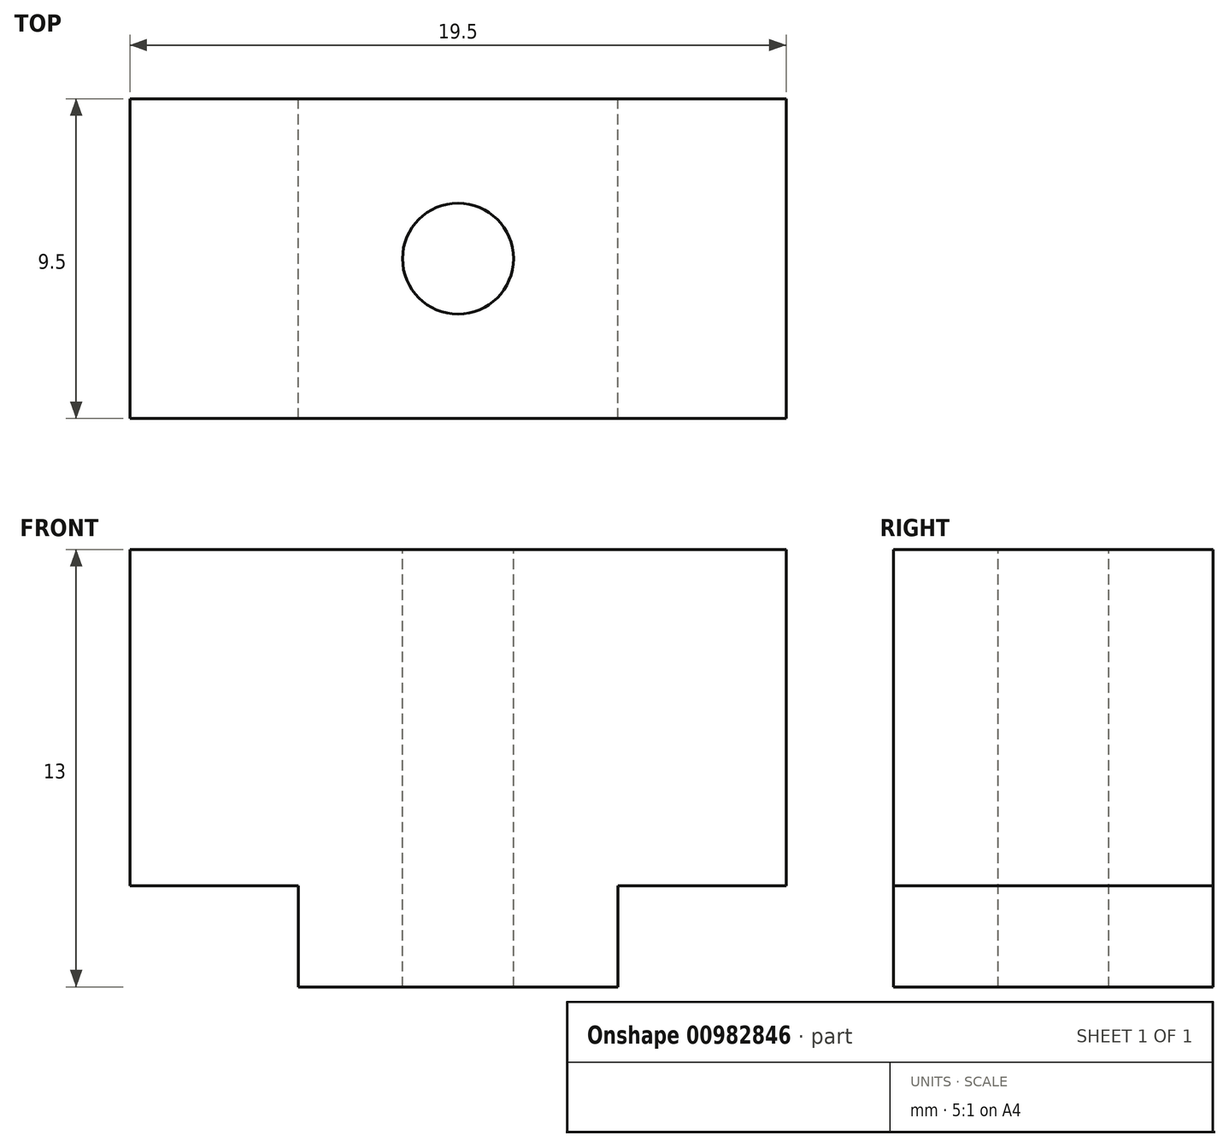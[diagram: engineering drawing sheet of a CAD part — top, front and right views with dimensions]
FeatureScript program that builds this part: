
annotation { "Feature Type Name" : "Feature", "Feature Type Description" : "" }
export const myFeature = defineFeature(function(context is Context, id is Id, definition is map)
    precondition{}
    {
        {
            var Q0;
            Q0=qCreatedBy(makeId("Front.planeOp"),FACE);
            var sketch = newSketch(context, id + "F0", { "sketchPlane" : qUnion([Q0])});
            skLineSegment(sketch, "E0", {"start": v(0, 10) * mm, "end": v(-9.75, 10) * mm});
            skLineSegment(sketch, "E1", {"start": v(-9.75, 10) * mm, "end": v(-9.75, 0) * mm});
            skLineSegment(sketch, "E2", {"start": v(-9.75, 0) * mm, "end": v(-4.75, 0) * mm});
            skLineSegment(sketch, "E3", {"start": v(-4.75, 0) * mm, "end": v(-4.75, -3) * mm});
            skLineSegment(sketch, "E4", {"start": v(-4.75, -3) * mm, "end": v(0, -3) * mm});
            skLineSegment(sketch, "E5.MirrorCS", {"start": v(0, 10) * mm, "end": v(9.75, 10) * mm});
            skLineSegment(sketch, "E6.MirrorCS", {"start": v(9.75, 10) * mm, "end": v(9.75, 0) * mm});
            skLineSegment(sketch, "E7.MirrorCS", {"start": v(9.75, 0) * mm, "end": v(4.75, 0) * mm});
            skLineSegment(sketch, "E8.MirrorCS", {"start": v(4.75, 0) * mm, "end": v(4.75, -3) * mm});
            skLineSegment(sketch, "E9.MirrorCS", {"start": v(4.75, -3) * mm, "end": v(0, -3) * mm});
            skSolve(sketch);
        }
        {
            var Q0;
            Q0 = qSketchRegion(id + "F0", true);
            extrude(context, id + "F1", {"entities" : qUnion([Q0]), "depth" : 9.5 * mm, "offsetDistance" : 25 * mm});
        }
        {
            var Q0;
            Q0=makeQuery(id+"F1.opExtrude","SWEPT_FACE",FACE,{"disambiguationData":[OSD([sQuery(id+"F0.wireOp",EDGE,"E0"),sQuery(id+"F0.wireOp",EDGE,"E5.MirrorCS")])]});
            var sketch = newSketch(context, id + "F2", { "sketchPlane" : qUnion([Q0])});
            skLineSegment(sketch, "E10", {"start": v(-9.75, 0) * mm, "end": v(9.75, -9.5) * mm, "construction": true});
            skLineSegment(sketch, "E11", {"start": v(9.75, 0) * mm, "end": v(-9.75, -9.5) * mm, "construction": true});
            skPoint(sketch, "E12", {"position": v(0, -4.75) * mm});
            skCircle(sketch, "E13", {"center": v(0, -4.75) * mm, "radius": 1.65 * mm});
            skSolve(sketch);
        }
        {
            var Q0;
            Q0=makeQuery(id+"F2.imprint","IMPRINT",FACE,{"disambiguationData":[TD([[makeQuery(id+"F2.imprint","IMPRINT",EDGE,{"derivedFrom":sQuery(id+"F2.wireOp",EDGE,"E13")}),1.0]])]});
            var Q1;
            Q1=sQuery(id+"F2.wireOp",EDGE,"E13");
            extrude(context, id + "F3", {"entities" : qUnion([Q0]), "operationType" : NewBodyOperationType.REMOVE, "surfaceEntities" : qUnion([Q1]), "endBound" : BoundingType.THROUGH_ALL, "oppositeDirection" : true, "depth" : 25 * mm, "offsetDistance" : 25 * mm});
        }
    });
